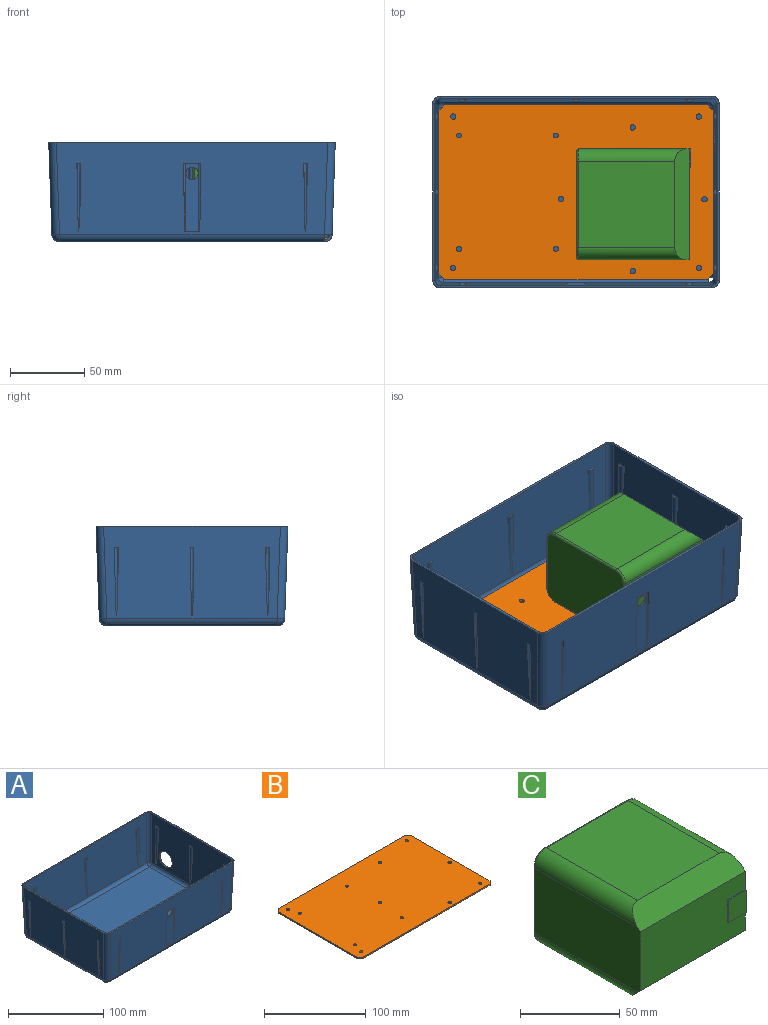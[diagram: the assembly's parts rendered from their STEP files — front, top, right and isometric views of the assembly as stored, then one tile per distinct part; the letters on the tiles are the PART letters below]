
ASSEMBLY  parts=3 mates=3
PART A: 98 faces, bbox 193.9x130.2x68.4 mm
  f0: cylinder r=1.14mm len=45.78mm, axis (0,0,1), area 127.7mm2, adj f75,f96
  f1: cylinder r=1.14mm len=45.78mm, axis (0,0,1), area 127.7mm2, adj f75,f95
  f2: cylinder r=1.14mm len=45.78mm, axis (0,0,1), area 127.7mm2, adj f75,f94
  f3: cylinder r=1.14mm len=45.89mm, axis (0,0,1), area 127.8mm2, adj f74,f93
  f4: cylinder r=1.14mm len=45.89mm, axis (0,0,1), area 127.8mm2, adj f74,f92
  f5: cylinder r=1.14mm len=45.89mm, axis (0,0,1), area 127.8mm2, adj f74,f91
  f6: cylinder r=1.14mm len=45.89mm, axis (0,0,1), area 127.8mm2, adj f70,f80
  f7: cylinder r=1.14mm len=45.89mm, axis (0,0,1), area 127.8mm2, adj f70,f79
  f8: cylinder r=1.14mm len=45.89mm, axis (0,0,1), area 127.8mm2, adj f70,f78
  f9: cylinder r=2.67mm len=47.28mm, axis (0,0,1), area 193.5mm2, adj f36,f63
  f10: cylinder r=2.67mm len=47.28mm, axis (0,0,1), area 193.5mm2, adj f36,f62
  f11: cylinder r=2.67mm len=47.28mm, axis (0,0,1), area 193.5mm2, adj f36,f61
  f12: bspline ~8.2x4.1mm, area 19.7mm2, adj f22,f50,f86
  f13: plane 182.38x1.52mm, normal (0,0.03,1), area 277.9mm2, adj f14,f23,f36,f75
  f14: bspline ~5.08x5.08mm, area 10.3mm2, adj f13,f15,f54,f90
  f15: plane 118.75x1.52mm, normal (-0.03,0,1), area 181mm2, adj f14,f16,f35,f74
  f16: bspline ~5.08x5.08mm, area 10.3mm2, adj f15,f17,f45,f81
  f17: plane 182.38x1.52mm, normal (0,-0.03,1), area 277.9mm2, adj f16,f18,f33,f72
  f18: bspline ~5.08x5.08mm, area 10.3mm2, adj f17,f19,f38,f77
  f19: plane 118.75x1.52mm, normal (0.03,0,1), area 181mm2, adj f18,f23,f31,f70
  f20: plane 5.08x4.96mm, normal (1,0,0), area 10.1mm2, adj f21,f24,f27,f66
  f21: plane 5.08x4.96mm, normal (0,-1,0), area 10.1mm2, adj f20,f24,f26,f65
  f22: bspline ~8.2x4.1mm, area 19.7mm2, adj f12,f50,f86
  f23: bspline ~5.08x5.08mm, area 10.3mm2, adj f13,f19,f37,f76
  f24: plane 5.08x5.08mm, normal (-0.03,0.03,-1), area 10.3mm2, adj f20,f21,f38,f77
  f25: plane 178.04x114.41mm, normal (0,0,1), area 20369.8mm2, adj f26,f27,f28,f29
  f26: cylinder r=3.56mm len=114.41mm, axis (0,-1,0), area 624.9mm2, adj f21,f25,f30,f31
  f27: cylinder r=3.56mm len=178.04mm, axis (-1,0,0), area 972.4mm2, adj f20,f25,f32,f33
  f28: cylinder r=3.56mm len=114.41mm, axis (0,1,0), area 624.9mm2, adj f25,f32,f34,f35
  f29: cylinder r=3.56mm len=178.04mm, axis (1,0,0), area 972.4mm2, adj f25,f30,f34,f36
  f30: sphere r=3.56mm, area 19mm2, adj f26,f29,f37
  f31: plane 120.08x63.43mm, normal (-1,0,0.03), area 6452.8mm2, adj f19,f26,f37,f38,f39,f40,f41,f42
  f32: sphere r=3.56mm, area 19mm2, adj f27,f28,f45
  f33: plane 182.38x62.1mm, normal (0,1,0.03), area 10249mm2, adj f17,f27,f38,f45,f46,f47,f48,f49
  f34: sphere r=3.56mm, area 19mm2, adj f28,f29,f54
  f35: plane 118.75x62.1mm, normal (1,0,0.03), area 6738mm2, adj f15,f28,f45,f54,f55,f56,f57,f58
  f36: plane 182.38x62.1mm, normal (0,-1,0.03), area 10691.6mm2, adj f9,f10,f11,f13,f29,f37,f54,f61
  f37: cylinder r=3.56mm len=62.15mm, axis (0.03,0.03,1), area 347mm2, adj f23,f30,f31,f36
  f38: cylinder r=3.56mm len=62.15mm, axis (0.03,-0.03,1), area 347mm2, adj f18,f24,f31,f33
  f39: plane 4.93x1.65mm, normal (0,0,1), area 5.9mm2, adj f31,f40
  f40: cylinder r=2.67mm len=47.43mm, axis (0,0,1), area 193.5mm2, adj f31,f39
  f41: plane 4.93x1.65mm, normal (0,0,1), area 5.9mm2, adj f31,f42
  f42: cylinder r=2.67mm len=47.43mm, axis (0,0,1), area 193.5mm2, adj f31,f41
  f43: plane 4.93x1.65mm, normal (0,0,1), area 5.9mm2, adj f31,f44
  f44: cylinder r=2.67mm len=47.43mm, axis (0,0,1), area 193.5mm2, adj f31,f43
  f45: cylinder r=3.56mm len=62.15mm, axis (-0.03,-0.03,1), area 347mm2, adj f16,f32,f33,f35
  f46: plane 4.93x1.65mm, normal (0,0,1), area 5.9mm2, adj f33,f47
  f47: cylinder r=2.67mm len=47.43mm, axis (0,0,1), area 193.5mm2, adj f33,f46
  f48: plane 4.93x1.65mm, normal (0,0,1), area 5.9mm2, adj f33,f49
  f49: cylinder r=2.67mm len=47.43mm, axis (0,0,1), area 193.5mm2, adj f33,f48
  f50: plane 47.28x9.36mm, normal (0,1,0), area 389.4mm2, adj f12,f22,f33,f51,f52,f53
  f51: cylinder r=2.67mm len=47.28mm, axis (0,0,1), area 96.8mm2, adj f33,f50,f52
  f52: plane 14.29x1.65mm, normal (0,0,1), area 21.3mm2, adj f33,f50,f51,f53
  f53: cylinder r=2.67mm len=47.28mm, axis (0,0,1), area 96.8mm2, adj f33,f50,f52
  f54: cylinder r=3.56mm len=62.15mm, axis (-0.03,0.03,1), area 347mm2, adj f14,f34,f35,f36
  f55: plane 4.93x1.65mm, normal (0,0,1), area 5.9mm2, adj f35,f56
  f56: cylinder r=2.67mm len=47.43mm, axis (0,0,1), area 193.5mm2, adj f35,f55
  f57: plane 4.93x1.65mm, normal (0,0,1), area 5.9mm2, adj f35,f58
  f58: cylinder r=2.67mm len=47.43mm, axis (0,0,1), area 193.5mm2, adj f35,f57
  f59: plane 4.93x1.65mm, normal (0,0,1), area 5.9mm2, adj f35,f60
  f60: cylinder r=2.67mm len=47.43mm, axis (0,0,1), area 193.5mm2, adj f35,f59
  f61: plane 4.93x1.65mm, normal (0,0,1), area 5.9mm2, adj f11,f36
  f62: plane 4.93x1.65mm, normal (0,0,1), area 5.9mm2, adj f10,f36
  f63: plane 4.93x1.65mm, normal (0,0,1), area 5.9mm2, adj f9,f36
  f64: plane 178.04x114.41mm, normal (0,0,-1), area 20369.8mm2, adj f65,f66,f67,f68
  f65: cylinder r=5.08mm len=114.41mm, axis (0,-1,0), area 892.7mm2, adj f21,f64,f69,f70
  f66: cylinder r=5.08mm len=178.04mm, axis (-1,0,0), area 1389.1mm2, adj f20,f64,f71,f72
  f67: cylinder r=5.08mm len=114.41mm, axis (0,1,0), area 892.7mm2, adj f64,f71,f73,f74
  f68: cylinder r=5.08mm len=178.04mm, axis (1,0,0), area 1389.1mm2, adj f64,f69,f73,f75
  f69: bspline ~5.08x5.08mm, area 38.8mm2, adj f65,f68,f76
  f70: plane 120.08x63.43mm, normal (1,0,-0.03), area 6695.4mm2, adj f6,f7,f8,f19,f65,f76,f77,f78
  f71: revolved ~5.08x5.08mm, area 38.8mm2, adj f66,f67,f81
  f72: plane 182.38x62.1mm, normal (0,-1,-0.03), area 10505.6mm2, adj f17,f66,f77,f81,f82,f83,f84,f85
  f73: revolved ~5.08x5.08mm, area 38.7mm2, adj f67,f68,f90
  f74: plane 119.04x62.39mm, normal (-1,0,-0.03), area 6980.6mm2, adj f3,f4,f5,f15,f67,f81,f90,f91
  f75: plane 182.38x62.1mm, normal (0,1,-0.03), area 10934.2mm2, adj f0,f1,f2,f13,f68,f76,f90,f94
  f76: cylinder r=5.08mm len=62.17mm, axis (0.03,0.03,1), area 495.8mm2, adj f23,f69,f70,f75
  f77: cylinder r=5.08mm len=62.17mm, axis (0.03,-0.03,1), area 495.8mm2, adj f18,f24,f70,f72
  f78: plane 2.29x1.6mm, normal (0,0,-1), area 3.1mm2, adj f8,f70
  f79: plane 2.29x1.6mm, normal (0,0,-1), area 3.1mm2, adj f7,f70
  f80: plane 2.29x1.6mm, normal (0,0,-1), area 3.1mm2, adj f6,f70
  f81: cylinder r=5.08mm len=62.17mm, axis (-0.03,-0.03,1), area 495.8mm2, adj f16,f71,f72,f74
  f82: plane 2.29x1.6mm, normal (0,0,-1), area 3.1mm2, adj f72,f83
  f83: cylinder r=1.14mm len=45.96mm, axis (0,0,1), area 127.7mm2, adj f72,f82
  f84: plane 2.29x1.6mm, normal (0,0,-1), area 3.1mm2, adj f72,f85
  f85: cylinder r=1.14mm len=45.96mm, axis (0,0,1), area 127.7mm2, adj f72,f84
  f86: plane 45.78x9.36mm, normal (0,-1,0), area 375.3mm2, adj f12,f22,f72,f87,f88,f89
  f87: cylinder r=1.14mm len=45.78mm, axis (0,0,1), area 63.9mm2, adj f72,f86,f88
  f88: plane 11.64x1.6mm, normal (0,0,-1), area 18mm2, adj f72,f86,f87,f89
  f89: cylinder r=1.14mm len=45.78mm, axis (0,0,1), area 63.9mm2, adj f72,f86,f88
  f90: cylinder r=5.08mm len=62.17mm, axis (-0.03,0.03,1), area 495.8mm2, adj f14,f73,f74,f75
  f91: plane 2.29x1.6mm, normal (0,0,-1), area 3.1mm2, adj f5,f74
  f92: plane 2.29x1.6mm, normal (0,0,-1), area 3.1mm2, adj f4,f74
  f93: plane 2.29x1.6mm, normal (0,0,-1), area 3.1mm2, adj f3,f74
  f94: plane 2.29x1.6mm, normal (0,0,-1), area 3.1mm2, adj f2,f75
  f95: plane 2.29x1.6mm, normal (0,0,-1), area 3.1mm2, adj f1,f75
  f96: plane 2.29x1.6mm, normal (0,0,-1), area 3.1mm2, adj f0,f75
  f97: cylinder r=9.53mm len=19.05mm, axis (-1,0,0), area 91.3mm2, adj f31,f70
PART B: 22 faces, bbox 184.2x117.5x1.5 mm
  f0: plane 176.53x1.52mm, normal (0,-1,0), area 269mm2, adj f4,f5,f11,f12
  f1: plane 109.86x1.52mm, normal (1,0,0), area 167.4mm2, adj f4,f5,f12,f13
  f2: plane 176.53x1.52mm, normal (0,1,0), area 269mm2, adj f4,f5,f10,f13
  f3: plane 109.86x1.52mm, normal (-1,0,0), area 167.4mm2, adj f4,f5,f10,f11
  f4: plane 184.15x117.48mm, normal (0,0,1), area 21488.6mm2, adj f0,f1,f2,f3,f6,f7,f8,f9
  f5: plane 184.15x117.48mm, normal (0,0,-1), area 21488.6mm2, adj f0,f1,f2,f3,f6,f7,f8,f9
  f6: cylinder r=1.78mm len=3.56mm, axis (0,0,1), area 17mm2, adj f4,f5
  f7: cylinder r=1.78mm len=3.56mm, axis (0,0,1), area 17mm2, adj f4,f5
  f8: cylinder r=1.78mm len=3.56mm, axis (0,0,1), area 17mm2, adj f4,f5
  f9: cylinder r=1.78mm len=3.56mm, axis (0,0,1), area 17mm2, adj f4,f5
  f10: plane 3.81x3.81mm, normal (-0.71,0.71,0), area 8.2mm2, adj f2,f3,f4,f5
  f11: plane 3.81x3.81mm, normal (-0.71,-0.71,0), area 8.2mm2, adj f0,f3,f4,f5
  f12: plane 3.81x3.81mm, normal (0.71,-0.71,0), area 8.2mm2, adj f0,f1,f4,f5
  f13: plane 3.81x3.81mm, normal (0.71,0.71,0), area 8.2mm2, adj f1,f2,f4,f5
  f14: cylinder r=1.66mm len=3.33mm, axis (0,0,1), area 15.9mm2, adj f4,f5
  f15: cylinder r=1.66mm len=3.33mm, axis (0,0,1), area 15.9mm2, adj f4,f5
  f16: cylinder r=1.66mm len=3.33mm, axis (0,0,1), area 15.9mm2, adj f4,f5
  f17: cylinder r=1.66mm len=3.33mm, axis (0,0,1), area 15.9mm2, adj f4,f5
  f18: cylinder r=1.8mm len=3.61mm, axis (0,0,1), area 17.3mm2, adj f4,f5
  f19: cylinder r=1.8mm len=3.61mm, axis (0,0,1), area 17.3mm2, adj f4,f5
  f20: cylinder r=1.8mm len=3.61mm, axis (0,0,1), area 17.3mm2, adj f4,f5
  f21: cylinder r=1.8mm len=3.61mm, axis (0,0,1), area 17.3mm2, adj f4,f5
PART C: 24 faces, bbox 75.8x76.6x57.9 mm
  f0: plane 74.42x36.2mm, normal (0,-1,0), area 2519.5mm2, adj f1,f3,f10,f11,f12,f13,f14
  f1: plane 75.31x40.01mm, normal (1,0,0), area 2992.5mm2, adj f0,f6,f8,f10,f11,f12,f13,f15
  f2: plane 71.88x53.98mm, normal (0,1,0), area 3837.9mm2, adj f16,f17,f18,f19,f20,f21,f22,f23
  f3: plane 74.68x40.01mm, normal (-1,0,0), area 2983.8mm2, adj f0,f7,f9,f10,f11,f20
  f4: plane 64.52x57.91mm, normal (0,0,-1), area 3736.3mm2, adj f8,f9,f10,f23
  f5: plane 64.52x57.91mm, normal (0,0,1), area 3736.3mm2, adj f6,f7,f11,f16
  f6: cylinder r=8.26mm len=72.77mm, axis (0,1,0), area 875.5mm2, adj f1,f5,f11,f17
  f7: cylinder r=8.26mm len=72.77mm, axis (0,-1,0), area 875.5mm2, adj f3,f5,f11,f18
  f8: cylinder r=8.26mm len=72.77mm, axis (0,-1,0), area 875.5mm2, adj f1,f4,f10,f21
  f9: cylinder r=8.26mm len=72.77mm, axis (0,1,0), area 875.5mm2, adj f3,f4,f10,f22
  f10: plane 74.42x10.16mm, normal (0,-0.71,-0.71), area 1028mm2, adj f0,f1,f3,f4,f8,f9
  f11: plane 74.42x10.16mm, normal (0,-0.71,0.71), area 1028mm2, adj f0,f1,f3,f5,f6,f7
  f12: plane 12.7x0.64mm, normal (0,0,-1), area 8.1mm2, adj f0,f1,f14,f15
  f13: plane 12.7x0.64mm, normal (0,0,1), area 8.1mm2, adj f0,f1,f14,f15
  f14: plane 13.72x0.64mm, normal (-1,0,0), area 8.7mm2, adj f0,f12,f13,f15
  f15: plane 13.72x12.7mm, normal (0,-1,0), area 174.2mm2, adj f1,f12,f13,f14
  f16: cylinder r=1.27mm len=57.91mm, axis (-1,0,0), area 115.5mm2, adj f2,f5,f17,f18
  f17: torus R=6.99mm, axis (0,1,0), area 24.4mm2, adj f2,f6,f16,f19
  f18: torus R=6.99mm, axis (0,1,0), area 24.4mm2, adj f2,f7,f16,f20
  f19: cylinder r=1.27mm len=40.01mm, axis (0,0,1), area 79.8mm2, adj f1,f2,f17,f21
  f20: cylinder r=1.27mm len=40.01mm, axis (0,0,-1), area 79.8mm2, adj f2,f3,f18,f22
  f21: torus R=6.99mm, axis (0,1,0), area 24.4mm2, adj f2,f8,f19,f23
  f22: torus R=6.99mm, axis (0,1,0), area 24.4mm2, adj f2,f9,f20,f23
  f23: cylinder r=1.27mm len=57.91mm, axis (1,0,0), area 115.5mm2, adj f2,f4,f21,f22
PLACE A t=(-0.55,-2.2,34.62)mm fixed
PLACE B t=(-0.55,-2.21,-30.91)mm
PLACE C rot(axis=(0,0,1),90deg) t=(37.96,-10.43,27.13)mm
MATE planar C.f4 <-> B.f4  axis (0,0,-1) through (33.52,-10.43,-29.39)mm
MATE planar B.f5 <-> A.f25  axis (0,0,-1) through (-0.55,-2.2,-30.91)mm
MATE fastened B.f5 <-> A.f25  axis (0,0,-1) through (-0.55,-2.2,-30.91)mm
